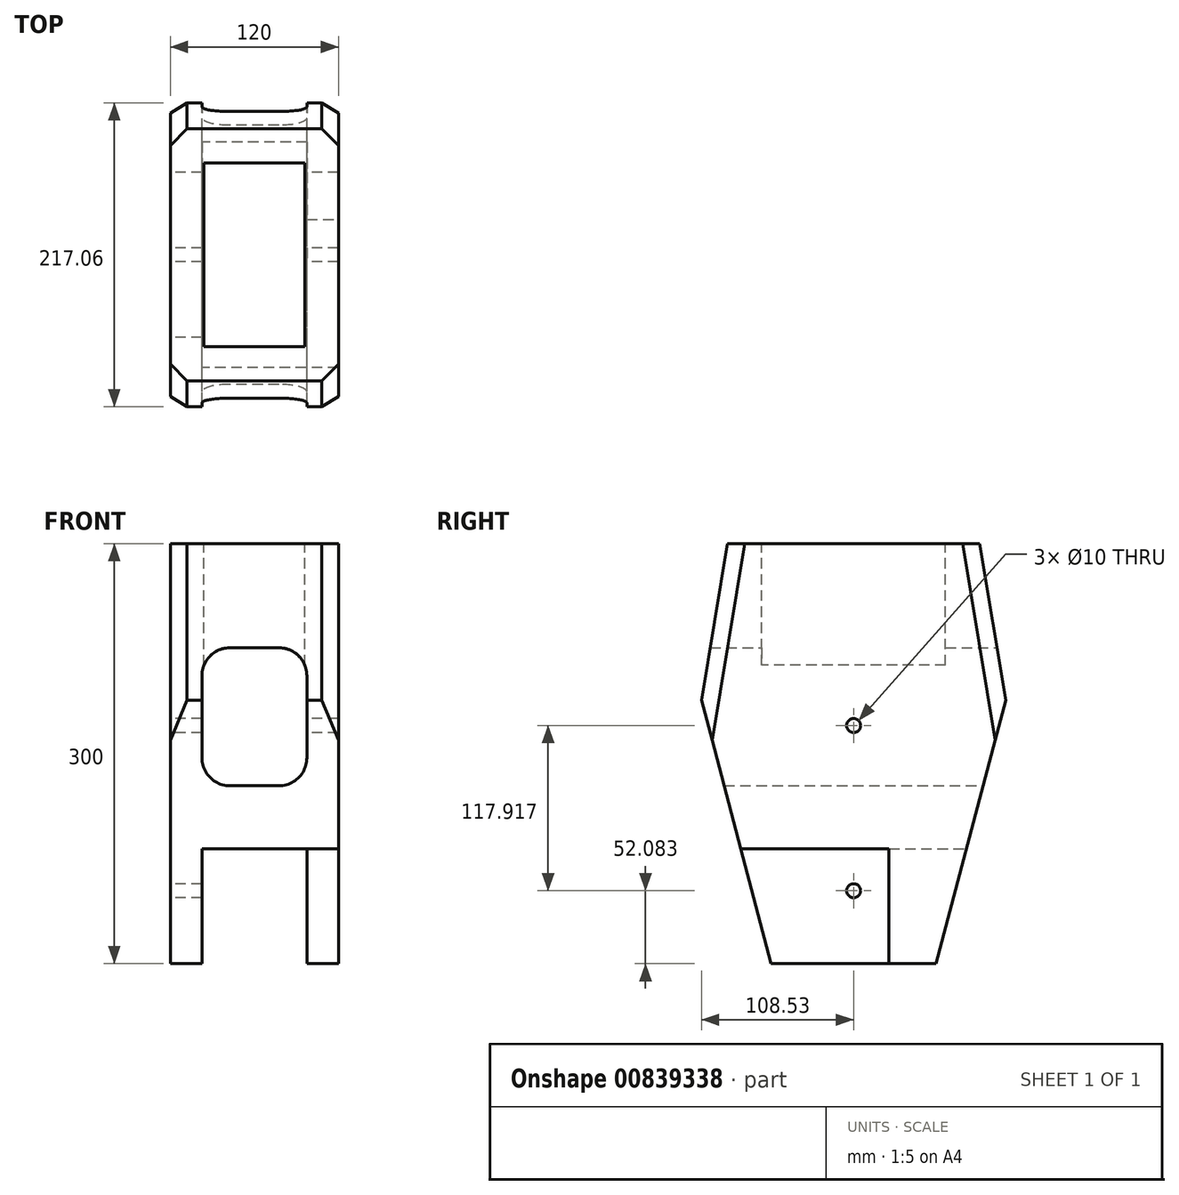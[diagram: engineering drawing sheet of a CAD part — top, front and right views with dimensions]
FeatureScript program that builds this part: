
annotation { "Feature Type Name" : "Feature", "Feature Type Description" : "" }
export const myFeature = defineFeature(function(context is Context, id is Id, definition is map)
    precondition{}
    {
        {
            var Q0;
            Q0=qCreatedBy(makeId("Right.planeOp"),FACE);
            var sketch = newSketch(context, id + "F0", { "sketchPlane" : qUnion([Q0])});
            skLineSegment(sketch, "E0", {"start": v(0, 455.61) * mm, "end": v(0, 200) * mm, "construction": true});
            skCircle(sketch, "E1", {"center": v(0, 0) * mm, "radius": 5 * mm});
            skCircle(sketch, "E2", {"center": v(0, -117.92) * mm, "radius": 5 * mm});
            skLineSegment(sketch, "E3", {"start": v(-75, -170) * mm, "end": v(-75, 130) * mm, "construction": true});
            skPoint(sketch, "E4.start.orphan", {"position": v(-75, 0) * mm});
            skLineSegment(sketch, "E5.MirrorCS", {"start": v(75, -170) * mm, "end": v(75, 130) * mm, "construction": true});
            skPoint(sketch, "E6.MirrorCS.end.orphan", {"position": v(75, -170) * mm});
            skPoint(sketch, "E6.MirrorCS.start.orphan", {"position": v(75, 0) * mm});
            skLineSegment(sketch, "E7", {"start": v(75, -170) * mm, "end": v(-75, -170) * mm, "construction": true});
            skPoint(sketch, "E8.MirrorCS.start.orphan", {"position": v(0, -170) * mm});
            skLineSegment(sketch, "E9", {"start": v(-75, 130) * mm, "end": v(75, 130) * mm});
            skLineSegment(sketch, "E10.trimOffspring", {"start": v(0, 195) * mm, "end": v(0, -170) * mm, "construction": true});
            skLineSegment(sketch, "E11", {"start": v(-75, 130) * mm, "end": v(-90, 130) * mm});
            skLineSegment(sketch, "E12", {"start": v(-90, 130) * mm, "end": v(-108.53, 17.94) * mm});
            skLineSegment(sketch, "E13.MirrorCS", {"start": v(75, 130) * mm, "end": v(90, 130) * mm});
            skLineSegment(sketch, "E14.MirrorCS", {"start": v(90, 130) * mm, "end": v(108.53, 17.94) * mm});
            skLineSegment(sketch, "E15", {"start": v(58.9, -170) * mm, "end": v(-58.9, -170) * mm});
            skLineSegment(sketch, "E16", {"start": v(-108.53, 17.94) * mm, "end": v(-58.9, -170) * mm});
            skLineSegment(sketch, "E17.MirrorCS", {"start": v(108.53, 17.94) * mm, "end": v(58.9, -170) * mm});
            skPoint(sketch, "E18.start.orphan", {"position": v(-75, -80.47) * mm});
            skPoint(sketch, "E19.MirrorCS.start.orphan", {"position": v(75, -80.47) * mm});
            skPoint(sketch, "E20.orphan", {"position": v(-36.3, -255.63) * mm});
            skPoint(sketch, "E21.orphan", {"position": v(36.3, -255.63) * mm});
            skSolve(sketch);
        }
        {
            var Q0;
            Q0=makeQuery(id+"F0.imprint","IMPRINT",FACE,{"disambiguationData":[TD([[makeQuery(id+"F0.imprint","IMPRINT",EDGE,{"derivedFrom":sQuery(id+"F0.wireOp",EDGE,"bJJHOdsB-26hl-RVyC-n3W4-FHLlQgOHxvKo")}),1.0]])]});
            var Q1;
            Q1=makeQuery(id+"F0.imprint","IMPRINT",FACE,{"disambiguationData":[TD([[makeQuery(id+"F0.imprint","IMPRINT",EDGE,{"derivedFrom":sQuery(id+"F0.wireOp",EDGE,"RGSMXENa-Ee4u-1fXq-X1ao-Yd9uJYyGhcAm")}),1.0]])]});
            var Q2;
            Q2=makeQuery(id+"F0.imprint","IMPRINT",FACE,{"disambiguationData":[TD([[makeQuery(id+"F0.imprint","IMPRINT",EDGE,{"derivedFrom":sQuery(id+"F0.wireOp",EDGE,"E1")}),-1.0]])]});
            extrude(context, id + "F1", {"entities" : qUnion([Q0, Q1, Q2]), "endBound" : BoundingType.SYMMETRIC, "depth" : 120 * mm, "offsetDistance" : 25 * mm});
        }
        {
            var Q0;
            Q0=qCreatedBy(makeId("Right.planeOp"),FACE);
            var sketch = newSketch(context, id + "F2", { "sketchPlane" : qUnion([Q0])});
            skLineSegment(sketch, "E22.bottom", {"start": v(-176.38, 169.99) * mm, "end": v(129.62, 169.99) * mm});
            skLineSegment(sketch, "E22.top", {"start": v(-176.38, -136.01) * mm, "end": v(129.62, -136.01) * mm});
            skLineSegment(sketch, "E22.left", {"start": v(-176.38, 169.99) * mm, "end": v(-176.38, -136.01) * mm});
            skLineSegment(sketch, "E22.right", {"start": v(129.62, 169.99) * mm, "end": v(129.62, -136.01) * mm});
            skSolve(sketch);
        }
        {
            var Q0;
            Q0=makeQuery(id+"F2.imprint","IMPRINT",FACE,{"disambiguationData":[TD([[makeQuery(id+"F2.imprint","IMPRINT",EDGE,{"derivedFrom":sQuery(id+"F2.wireOp",EDGE,"E22.bottom")}),-1.0]])]});
            var sketch = newSketch(context, id + "F3", { "sketchPlane" : qUnion([Q0])});
            skLineSegment(sketch, "E23.bottom", {"start": v(-145.45, 55.55) * mm, "end": v(163.91, 55.55) * mm});
            skLineSegment(sketch, "E23.top", {"start": v(-145.45, -228.9) * mm, "end": v(163.91, -228.9) * mm});
            skLineSegment(sketch, "E23.left", {"start": v(-145.45, 55.55) * mm, "end": v(-145.45, -228.9) * mm});
            skLineSegment(sketch, "E23.right", {"start": v(163.91, 55.55) * mm, "end": v(163.91, -228.9) * mm});
            skSolve(sketch);
        }
        {
            var Q0;
            Q0 = qSketchRegion(id + "F3", true);
            extrude(context, id + "F4", {"entities" : qUnion([Q0]), "operationType" : NewBodyOperationType.REMOVE, "endBound" : BoundingType.SYMMETRIC, "depth" : 75 * mm, "offsetDistance" : 25 * mm});
        }
        {
            var Q0;
            Q0=makeQuery(id+"F1.opExtrude","CAP_EDGE",EDGE,{"disambiguationData":[OSD([sQuery(id+"F0.wireOp",EDGE,"E12")])],"isStart":true});
            var Q1;
            Q1=makeQuery(id+"F1.opExtrude","CAP_EDGE",EDGE,{"disambiguationData":[OSD([sQuery(id+"F0.wireOp",EDGE,"E14.MirrorCS")])],"isStart":true});
            var Q2;
            Q2=makeQuery(id+"F1.opExtrude","CAP_EDGE",EDGE,{"disambiguationData":[OSD([sQuery(id+"F0.wireOp",EDGE,"E12")])],"isStart":false});
            var Q3;
            Q3=makeQuery(id+"F1.opExtrude","CAP_EDGE",EDGE,{"disambiguationData":[OSD([sQuery(id+"F0.wireOp",EDGE,"E14.MirrorCS")])],"isStart":false});
            chamfer(context, id + "F5", {"entities" : qUnion([Q0, Q1, Q2, Q3]), "width" : 12 * mm, "tangentPropagation" : true});
        }
        {
            var Q0;
            Q0=makeQuery(id+"F4.boolean.opBoolean","COPY",FACE,{"derivedFrom":makeQuery(id+"F4.opExtrude","CAP_FACE",FACE,{"disambiguationData":[OSD([sQuery(id+"F3.wireOp",EDGE,"E23.bottom"),sQuery(id+"F3.wireOp",EDGE,"E23.top"),sQuery(id+"F3.wireOp",EDGE,"E23.left"),sQuery(id+"F3.wireOp",EDGE,"E23.right")])],"isStart":true})});
            var sketch = newSketch(context, id + "F6", { "sketchPlane" : qUnion([Q0])});
            skLineSegment(sketch, "E24.0", {"start": v(-92.44, -43) * mm, "end": v(-80.53, -88.07) * mm});
            skLineSegment(sketch, "E25.0", {"start": v(92.44, -43) * mm, "end": v(80.53, -88.07) * mm});
            skLineSegment(sketch, "E26", {"start": v(-92.44, -43) * mm, "end": v(92.44, -43) * mm});
            skLineSegment(sketch, "E27", {"start": v(-80.53, -88.07) * mm, "end": v(80.53, -88.07) * mm});
            skPoint(sketch, "E28.orphan", {"position": v(-108.53, 17.94) * mm});
            skPoint(sketch, "E29.orphan", {"position": v(108.53, 17.94) * mm});
            skPoint(sketch, "E30.orphan", {"position": v(58.9, -170) * mm});
            skPoint(sketch, "E31.orphan", {"position": v(-58.9, -170) * mm});
            skSolve(sketch);
        }
        {
            var Q0;
            Q0=makeQuery(id+"F6.imprint","IMPRINT",FACE,{"disambiguationData":[TD([[makeQuery(id+"F6.imprint","IMPRINT",EDGE,{"derivedFrom":sQuery(id+"F6.wireOp",EDGE,"E24.0")}),1.0]])]});
            var Q1;
            Q1=makeQuery(id+"F4.boolean.opBoolean","COPY",FACE,{"derivedFrom":makeQuery(id+"F4.opExtrude","CAP_FACE",FACE,{"disambiguationData":[OSD([sQuery(id+"F3.wireOp",EDGE,"E23.bottom"),sQuery(id+"F3.wireOp",EDGE,"E23.top"),sQuery(id+"F3.wireOp",EDGE,"E23.left"),sQuery(id+"F3.wireOp",EDGE,"E23.right")])],"isStart":false})});
            extrude(context, id + "F7", {"entities" : qUnion([Q0]), "operationType" : NewBodyOperationType.ADD, "endBound" : BoundingType.UP_TO_SURFACE, "depth" : 25 * mm, "endBoundEntityFace" : qUnion([Q1]), "offsetDistance" : 25 * mm});
        }
        {
            var Q0;
            Q0=makeQuery(id+"F1.opExtrude","CAP_FACE",FACE,{"disambiguationData":[OSD([sQuery(id+"F0.wireOp",EDGE,"E1"),sQuery(id+"F0.wireOp",EDGE,"E2"),sQuery(id+"F0.wireOp",EDGE,"E9"),sQuery(id+"F0.wireOp",EDGE,"E11"),sQuery(id+"F0.wireOp",EDGE,"E12"),sQuery(id+"F0.wireOp",EDGE,"E13.MirrorCS"),sQuery(id+"F0.wireOp",EDGE,"E14.MirrorCS"),sQuery(id+"F0.wireOp",EDGE,"E15"),sQuery(id+"F0.wireOp",EDGE,"E16"),sQuery(id+"F0.wireOp",EDGE,"E17.MirrorCS")])],"isStart":false});
            var sketch = newSketch(context, id + "F8", { "sketchPlane" : qUnion([Q0])});
            skLineSegment(sketch, "E32.0", {"start": v(-101.05, -10.38) * mm, "end": v(-58.9, -170) * mm});
            skLineSegment(sketch, "E32.1", {"start": v(25.27, -170) * mm, "end": v(-58.9, -170) * mm});
            skLineSegment(sketch, "E33.0", {"start": v(-80.53, -88.07) * mm, "end": v(25.27, -88.07) * mm});
            skLineSegment(sketch, "E34", {"start": v(25.27, -170) * mm, "end": v(25.27, -88.07) * mm});
            skPoint(sketch, "E35.orphan", {"position": v(80.53, -88.07) * mm});
            skPoint(sketch, "E36.orphan", {"position": v(58.9, -170) * mm});
            skSolve(sketch);
        }
        {
            var Q0;
            Q0=makeQuery(id+"F4.boolean.opBoolean","COPY",EDGE,{"derivedFrom":makeQuery(id+"F4.opExtrude","CAP_EDGE",EDGE,{"disambiguationData":[OSD([sQuery(id+"F3.wireOp",EDGE,"E23.bottom")])],"isStart":true})});
            var Q1;
            Q1=makeQuery(id+"F4.boolean.opBoolean","COPY",EDGE,{"derivedFrom":makeQuery(id+"F4.opExtrude","CAP_EDGE",EDGE,{"disambiguationData":[OSD([sQuery(id+"F3.wireOp",EDGE,"E23.bottom")])],"isStart":false})});
            var Q2;
            Q2=makeQuery(id+"F7.opExtrude","CAP_EDGE",EDGE,{"disambiguationData":[OSD([sQuery(id+"F6.wireOp",EDGE,"E26")])],"isStart":true});
            var Q3;
            Q3=makeQuery(id+"F7.opExtrude","CAP_EDGE",EDGE,{"disambiguationData":[OSD([sQuery(id+"F6.wireOp",EDGE,"E26")])],"isStart":false});
            fillet(context, id + "F9", {"entities" : qUnion([Q0, Q1, Q2, Q3]), "radius" : 20 * mm, "tangentPropagation" : true, "allowEdgeOverflow" : false});
        }
        {
            var Q0;
            Q0=makeQuery(id+"F1.opExtrude","SWEPT_FACE",FACE,{"disambiguationData":[OSD([sQuery(id+"F0.wireOp",EDGE,"E9"),sQuery(id+"F0.wireOp",EDGE,"E11"),sQuery(id+"F0.wireOp",EDGE,"E13.MirrorCS")])]});
            var sketch = newSketch(context, id + "F10", { "sketchPlane" : qUnion([Q0])});
            skLineSegment(sketch, "E37", {"start": v(0, -90) * mm, "end": v(0, 90) * mm, "construction": true});
            skLineSegment(sketch, "E38", {"start": v(-60, 0) * mm, "end": v(60, 0) * mm, "construction": true});
            skLineSegment(sketch, "E39", {"start": v(0, 65.6) * mm, "end": v(-36.04, 65.6) * mm});
            skLineSegment(sketch, "E40", {"start": v(-36.04, 65.6) * mm, "end": v(-36.04, 0) * mm});
            skLineSegment(sketch, "E41.MirrorCS", {"start": v(0, 65.6) * mm, "end": v(36.04, 65.6) * mm});
            skLineSegment(sketch, "E42.MirrorCS", {"start": v(36.04, 65.6) * mm, "end": v(36.04, 0) * mm});
            skLineSegment(sketch, "E43.MirrorCS", {"start": v(-36.04, -65.6) * mm, "end": v(-36.04, 0) * mm});
            skLineSegment(sketch, "E44.MirrorCS", {"start": v(0, -65.6) * mm, "end": v(-36.04, -65.6) * mm});
            skLineSegment(sketch, "E45.MirrorCS", {"start": v(36.04, -65.6) * mm, "end": v(36.04, 0) * mm});
            skLineSegment(sketch, "E46.MirrorCS", {"start": v(0, -65.6) * mm, "end": v(36.04, -65.6) * mm});
            skSolve(sketch);
        }
        {
            var Q0;
            Q0 = qSketchRegion(id + "F10", true);
            extrude(context, id + "F11", {"entities" : qUnion([Q0]), "operationType" : NewBodyOperationType.REMOVE, "endBound" : BoundingType.UP_TO_NEXT, "oppositeDirection" : true, "depth" : 25 * mm, "offsetDistance" : 25 * mm});
        }
        {
            var Q0;
            {var subQ1=sQuery(id+"F8.wireOp",EDGE,"E32.1");Q0=makeQuery(id+"F8.imprint","IMPRINT",FACE,{"disambiguationData":[TD([[makeQuery(id+"F8.imprint","IMPRINT",EDGE,{"derivedFrom":subQ1}),-1.0]])]});}
            var Q1;
            Q1=makeQuery(id+"F7.boolean.opBoolean","SPLIT",FACE,{"disambiguationData":[TD([makeQuery(id+"F1.opExtrude","SWEPT_FACE",FACE,{"disambiguationData":[OSD([sQuery(id+"F0.wireOp",EDGE,"E2")])]})])],"derivedFrom":makeQuery(id+"F4.boolean.opBoolean","COPY",FACE,{"derivedFrom":makeQuery(id+"F4.opExtrude","CAP_FACE",FACE,{"disambiguationData":[OSD([sQuery(id+"F3.wireOp",EDGE,"E23.bottom"),sQuery(id+"F3.wireOp",EDGE,"E23.top"),sQuery(id+"F3.wireOp",EDGE,"E23.left"),sQuery(id+"F3.wireOp",EDGE,"E23.right")])],"isStart":false})})});
            extrude(context, id + "F12", {"entities" : qUnion([Q0, Q1]), "operationType" : NewBodyOperationType.REMOVE, "endBound" : BoundingType.UP_TO_NEXT, "oppositeDirection" : true, "depth" : 25 * mm, "offsetDistance" : 25 * mm});
        }
    });
